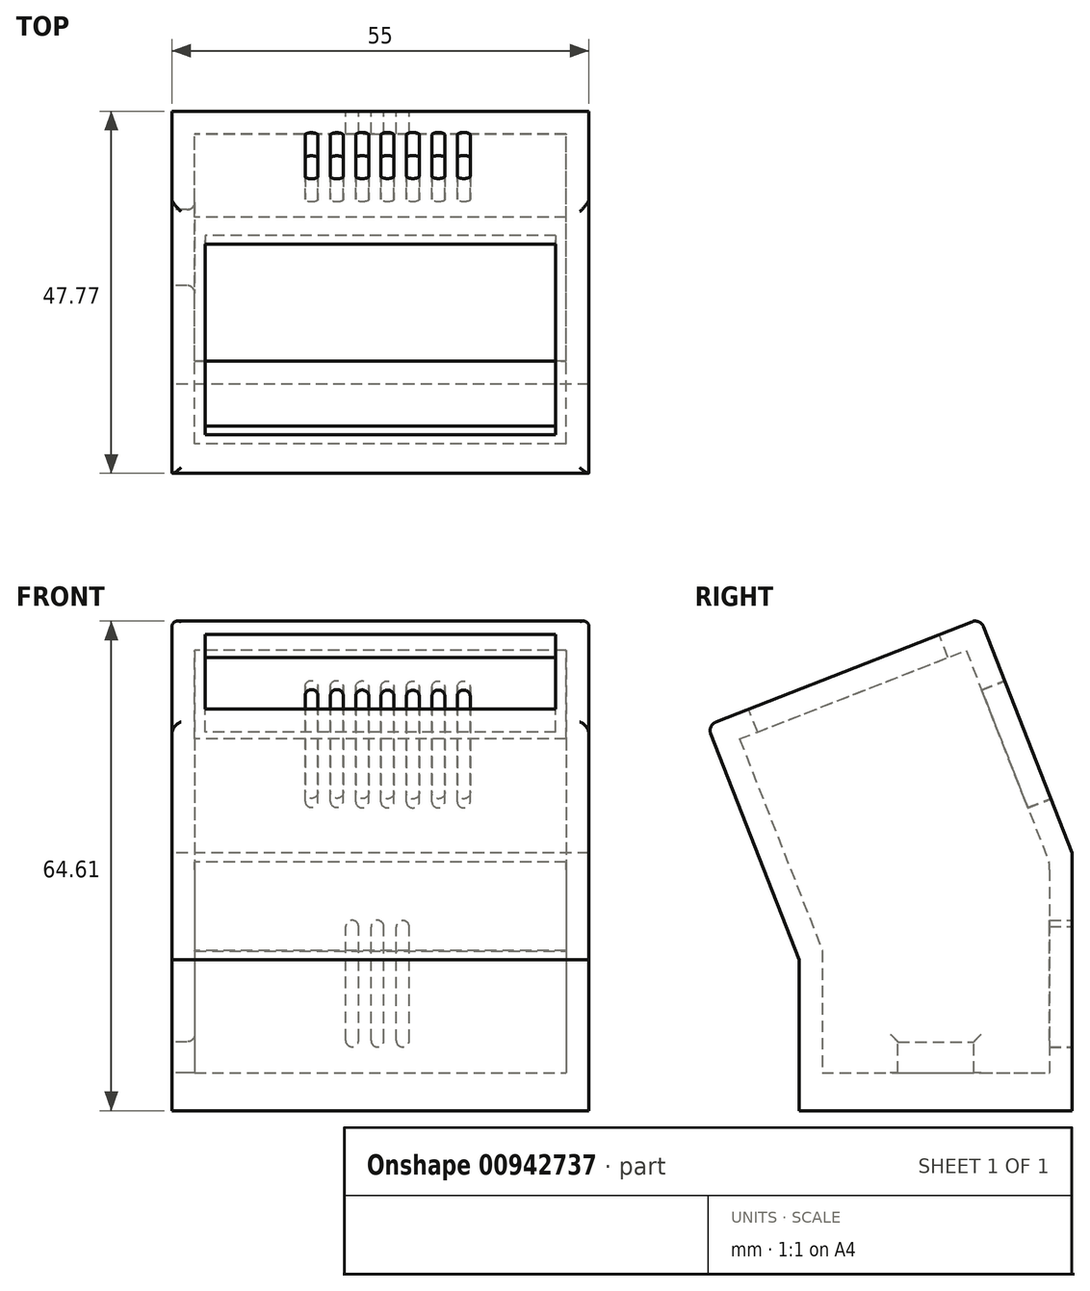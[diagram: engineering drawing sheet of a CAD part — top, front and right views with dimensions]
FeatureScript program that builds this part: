
annotation { "Feature Type Name" : "Feature", "Feature Type Description" : "" }
export const myFeature = defineFeature(function(context is Context, id is Id, definition is map)
    precondition{}
    {
        {
            var Q0;
            Q0=qCreatedBy(makeId("Top.planeOp"),FACE);
            var sketch = newSketch(context, id + "F0", { "sketchPlane" : qUnion([Q0])});
            skLineSegment(sketch, "E0.bottom", {"start": v(27.5, -18) * mm, "end": v(-27.5, -18) * mm});
            skLineSegment(sketch, "E0.top", {"start": v(27.5, 18) * mm, "end": v(-27.5, 18) * mm});
            skLineSegment(sketch, "E0.left", {"start": v(27.5, -18) * mm, "end": v(27.5, 18) * mm});
            skLineSegment(sketch, "E0.right", {"start": v(-27.5, -18) * mm, "end": v(-27.5, 18) * mm});
            skLineSegment(sketch, "E1.bottom", {"start": v(24.5, 15) * mm, "end": v(-24.5, 15) * mm});
            skLineSegment(sketch, "E1.top", {"start": v(24.5, -15) * mm, "end": v(-24.5, -15) * mm});
            skLineSegment(sketch, "E1.left", {"start": v(24.5, 15) * mm, "end": v(24.5, -15) * mm});
            skLineSegment(sketch, "E1.right", {"start": v(-24.5, 15) * mm, "end": v(-24.5, -15) * mm});
            skPoint(sketch, "E1.middle", {"position": v(0, 0) * mm});
            skSolve(sketch);
        }
        {
            var Q0;
            Q0 = qSketchRegion(id + "F0", true);
            extrude(context, id + "F1", {"entities" : qUnion([Q0]), "depth" : 34 * mm, "offsetDistance" : 25 * mm});
        }
        {
            var Q0;
            Q0=makeQuery(id+"F1.opExtrude","CAP_EDGE",EDGE,{"disambiguationData":[OSD([sQuery(id+"F0.wireOp",EDGE,"E0.bottom")])],"isStart":false});
            chamfer(context, id + "F2", {"entities" : qUnion([Q0]), "chamferType" : ChamferType.TWO_OFFSETS, "width1" : 14.1 * mm, "oppositeDirection" : false, "width2" : 36 * mm, "tangentPropagation" : true});
        }
        {
            var Q0;
            Q0=makeQuery(id+"F2.opChamfer","BLEND_FACE",FACE,{"disambiguationData":[OSD([sQuery(id+"F0.wireOp",EDGE,"E0.bottom")])]});
            var sketch = newSketch(context, id + "F3", { "sketchPlane" : qUnion([Q0])});
            skLineSegment(sketch, "E2.bottom", {"start": v(-27.5, 29.16) * mm, "end": v(27.5, 29.16) * mm});
            skLineSegment(sketch, "E2.top", {"start": v(-27.5, -9.5) * mm, "end": v(27.5, -9.5) * mm});
            skLineSegment(sketch, "E2.left", {"start": v(-27.5, 29.16) * mm, "end": v(-27.5, -9.5) * mm});
            skLineSegment(sketch, "E2.right", {"start": v(27.5, 29.16) * mm, "end": v(27.5, -9.5) * mm});
            skLineSegment(sketch, "E3.bottom", {"start": v(24.5, -6.22) * mm, "end": v(-24.5, -6.22) * mm});
            skLineSegment(sketch, "E3.top", {"start": v(24.5, 25.88) * mm, "end": v(-24.5, 25.88) * mm});
            skLineSegment(sketch, "E3.left", {"start": v(24.5, -6.22) * mm, "end": v(24.5, 25.88) * mm});
            skLineSegment(sketch, "E3.right", {"start": v(-24.5, -6.22) * mm, "end": v(-24.5, 25.88) * mm});
            skPoint(sketch, "E3.middle", {"position": v(0, 9.83) * mm});
            skPoint(sketch, "E3.middle.positionSnap0", {"position": v(-27.5, 9.83) * mm});
            skPoint(sketch, "E3.middle.positionSnap1", {"position": v(0, 29.16) * mm});
            skPoint(sketch, "E3.centerSnap0", {"position": v(-27.5, 9.83) * mm});
            skPoint(sketch, "E3.centerSnap1", {"position": v(0, 29.16) * mm});
            skSolve(sketch);
        }
        {
            var Q0;
            Q0 = qSketchRegion(id + "F3", true);
            extrude(context, id + "F4", {"entities" : qUnion([Q0]), "operationType" : NewBodyOperationType.ADD, "depth" : 30 * mm, "offsetDistance" : 25 * mm});
        }
        {
            var Q0;
            Q0=makeQuery(id+"F1.opExtrude","CAP_FACE",FACE,{"disambiguationData":[OSD([sQuery(id+"F0.wireOp",EDGE,"E0.bottom"),sQuery(id+"F0.wireOp",EDGE,"E0.top"),sQuery(id+"F0.wireOp",EDGE,"E0.left"),sQuery(id+"F0.wireOp",EDGE,"E0.right")])],"isStart":true});
            var sketch = newSketch(context, id + "F5", { "sketchPlane" : qUnion([Q0])});
            skLineSegment(sketch, "E4.bottom", {"start": v(24.5, -15) * mm, "end": v(-24.5, -15) * mm});
            skLineSegment(sketch, "E4.top", {"start": v(24.5, 15) * mm, "end": v(-24.5, 15) * mm});
            skLineSegment(sketch, "E4.left", {"start": v(24.5, -15) * mm, "end": v(24.5, 15) * mm});
            skLineSegment(sketch, "E4.right", {"start": v(-24.5, -15) * mm, "end": v(-24.5, 15) * mm});
            skPoint(sketch, "E4.middle", {"position": v(0, 0) * mm});
            skSolve(sketch);
        }
        {
            var Q0;
            {var subQ10=sQuery(id+"F5.wireOp",EDGE,"E4.bottom");Q0=makeQuery(id+"F5.imprint","IMPRINT",FACE,{"disambiguationData":[TD([[makeQuery(id+"F5.imprint","IMPRINT",EDGE,{"derivedFrom":subQ10}),1.0]])]});}
            var Q1;
            Q1 = qSketchRegion(id + "F5", true);
            extrude(context, id + "F6", {"entities" : qUnion([Q0, Q1]), "operationType" : NewBodyOperationType.ADD, "oppositeDirection" : true, "depth" : 5 * mm, "offsetDistance" : 25 * mm});
        }
        {
            var Q0;
            Q0=makeQuery(id+"F4.boolean.opBoolean","MERGE",FACE,{"derivedFrom":[makeQuery(id+"F1.opExtrude","SWEPT_FACE",FACE,{"disambiguationData":[OSD([sQuery(id+"F0.wireOp",EDGE,"E0.right")])]}),makeQuery(id+"F4.opExtrude","SWEPT_FACE",FACE,{"disambiguationData":[OSD([sQuery(id+"F3.wireOp",EDGE,"E2.left")])]})]});
            var sketch = newSketch(context, id + "F7", { "sketchPlane" : qUnion([Q0])});
            skLineSegment(sketch, "E5.bottom", {"start": v(5, 5) * mm, "end": v(-5, 5) * mm});
            skLineSegment(sketch, "E5.top", {"start": v(5, 9.08) * mm, "end": v(-5, 9.08) * mm});
            skLineSegment(sketch, "E5.left", {"start": v(5, 5) * mm, "end": v(5, 9.08) * mm});
            skLineSegment(sketch, "E5.right", {"start": v(-5, 5) * mm, "end": v(-5, 9.08) * mm});
            skPoint(sketch, "E5.middle", {"position": v(0, 7.04) * mm});
            skSolve(sketch);
        }
        {
            var Q0;
            Q0 = qSketchRegion(id + "F7", true);
            extrude(context, id + "F8", {"entities" : qUnion([Q0]), "operationType" : NewBodyOperationType.REMOVE, "oppositeDirection" : true, "depth" : 17.9 * mm, "offsetDistance" : 25 * mm});
        }
        {
            var Q0;
            Q0=makeQuery(id+"F8.boolean.opBoolean","INTERSECT",EDGE,{"derivedFrom":[makeQuery(id+"F4.boolean.opBoolean","MERGE",FACE,{"derivedFrom":[makeQuery(id+"F1.opExtrude","SWEPT_FACE",FACE,{"disambiguationData":[OSD([sQuery(id+"F0.wireOp",EDGE,"E1.right")])]}),makeQuery(id+"F4.opExtrude","SWEPT_FACE",FACE,{"disambiguationData":[OSD([sQuery(id+"F3.wireOp",EDGE,"E3.right")])]})]}),makeQuery(id+"F8.opExtrude","SWEPT_FACE",FACE,{"disambiguationData":[OSD([sQuery(id+"F7.wireOp",EDGE,"E5.right")])]})]});
            var Q1;
            Q1=makeQuery(id+"F8.boolean.opBoolean","INTERSECT",EDGE,{"derivedFrom":[makeQuery(id+"F4.boolean.opBoolean","MERGE",FACE,{"derivedFrom":[makeQuery(id+"F1.opExtrude","SWEPT_FACE",FACE,{"disambiguationData":[OSD([sQuery(id+"F0.wireOp",EDGE,"E1.right")])]}),makeQuery(id+"F4.opExtrude","SWEPT_FACE",FACE,{"disambiguationData":[OSD([sQuery(id+"F3.wireOp",EDGE,"E3.right")])]})]}),makeQuery(id+"F8.opExtrude","SWEPT_FACE",FACE,{"disambiguationData":[OSD([sQuery(id+"F7.wireOp",EDGE,"E5.left")])]})]});
            var Q2;
            Q2=makeQuery(id+"F8.boolean.opBoolean","INTERSECT",EDGE,{"derivedFrom":[makeQuery(id+"F4.boolean.opBoolean","MERGE",FACE,{"derivedFrom":[makeQuery(id+"F1.opExtrude","SWEPT_FACE",FACE,{"disambiguationData":[OSD([sQuery(id+"F0.wireOp",EDGE,"E1.right")])]}),makeQuery(id+"F4.opExtrude","SWEPT_FACE",FACE,{"disambiguationData":[OSD([sQuery(id+"F3.wireOp",EDGE,"E3.right")])]})]}),makeQuery(id+"F8.opExtrude","SWEPT_FACE",FACE,{"disambiguationData":[OSD([sQuery(id+"F7.wireOp",EDGE,"E5.top")])]})]});
            var Q3;
            Q3=makeQuery(id+"F8.boolean.opBoolean","COPY",EDGE,{"derivedFrom":makeQuery(id+"F8.opExtrude","CAP_EDGE",EDGE,{"disambiguationData":[OSD([sQuery(id+"F7.wireOp",EDGE,"E5.right")])],"isStart":true})});
            var Q4;
            Q4=makeQuery(id+"F8.boolean.opBoolean","COPY",EDGE,{"derivedFrom":makeQuery(id+"F8.opExtrude","CAP_EDGE",EDGE,{"disambiguationData":[OSD([sQuery(id+"F7.wireOp",EDGE,"E5.top")])],"isStart":true})});
            var Q5;
            Q5=makeQuery(id+"F8.boolean.opBoolean","COPY",EDGE,{"derivedFrom":makeQuery(id+"F8.opExtrude","CAP_EDGE",EDGE,{"disambiguationData":[OSD([sQuery(id+"F7.wireOp",EDGE,"E5.left")])],"isStart":true})});
            var Q6;
            Q6=makeQuery(id+"F8.boolean.opBoolean","COPY",EDGE,{"derivedFrom":makeQuery(id+"F8.opExtrude","CAP_EDGE",EDGE,{"disambiguationData":[OSD([sQuery(id+"F7.wireOp",EDGE,"E5.bottom")])],"isStart":true})});
            fillet(context, id + "F9", {"entities" : qUnion([Q0, Q1, Q2, Q3, Q4, Q5, Q6]), "radius" : 1 * mm, "tangentPropagation" : true, "allowEdgeOverflow" : false});
        }
        {
            var Q0;
            Q0=makeQuery(id+"F4.opExtrude","CAP_FACE",FACE,{"disambiguationData":[OSD([sQuery(id+"F3.wireOp",EDGE,"E2.bottom"),sQuery(id+"F3.wireOp",EDGE,"E2.top"),sQuery(id+"F3.wireOp",EDGE,"E2.left"),sQuery(id+"F3.wireOp",EDGE,"E2.right"),sQuery(id+"F3.wireOp",EDGE,"E3.bottom"),sQuery(id+"F3.wireOp",EDGE,"E3.top"),sQuery(id+"F3.wireOp",EDGE,"E3.left"),sQuery(id+"F3.wireOp",EDGE,"E3.right")])],"isStart":false});
            var sketch = newSketch(context, id + "F10", { "sketchPlane" : qUnion([Q0])});
            skLineSegment(sketch, "E6.bottom", {"start": v(-27.5, 29.16) * mm, "end": v(27.5, 29.16) * mm});
            skLineSegment(sketch, "E6.top", {"start": v(-27.5, -9.5) * mm, "end": v(27.5, -9.5) * mm});
            skLineSegment(sketch, "E6.left", {"start": v(-27.5, 29.16) * mm, "end": v(-27.5, -9.5) * mm});
            skLineSegment(sketch, "E6.right", {"start": v(27.5, 29.16) * mm, "end": v(27.5, -9.5) * mm});
            skSolve(sketch);
        }
        {
            var Q0;
            Q0 = qSketchRegion(id + "F10", true);
            extrude(context, id + "F11", {"entities" : qUnion([Q0]), "operationType" : NewBodyOperationType.ADD, "depth" : 3.25 * mm, "offsetDistance" : 25 * mm});
        }
        {
            var Q0;
            Q0=makeQuery(id+"F11.opExtrude","CAP_FACE",FACE,{"disambiguationData":[OSD([sQuery(id+"F10.wireOp",EDGE,"E6.bottom"),sQuery(id+"F10.wireOp",EDGE,"E6.top"),sQuery(id+"F10.wireOp",EDGE,"E6.left"),sQuery(id+"F10.wireOp",EDGE,"E6.right")])],"isStart":false});
            var sketch = newSketch(context, id + "F12", { "sketchPlane" : qUnion([Q0])});
            skLineSegment(sketch, "E7.bottom", {"start": v(23.12, -3.69) * mm, "end": v(-23.13, -3.69) * mm});
            skLineSegment(sketch, "E7.top", {"start": v(23.12, 23.31) * mm, "end": v(-23.13, 23.31) * mm});
            skLineSegment(sketch, "E7.left", {"start": v(23.12, -3.69) * mm, "end": v(23.12, 23.31) * mm});
            skLineSegment(sketch, "E7.right", {"start": v(-23.13, -3.69) * mm, "end": v(-23.13, 23.31) * mm});
            skPoint(sketch, "E7.middle", {"position": v(0, 9.81) * mm});
            skSolve(sketch);
        }
        {
            var Q0;
            Q0 = qSketchRegion(id + "F12", true);
            extrude(context, id + "F13", {"entities" : qUnion([Q0]), "operationType" : NewBodyOperationType.REMOVE, "oppositeDirection" : true, "depth" : 6.9 * mm, "offsetDistance" : 25 * mm});
        }
        {
            var Q0;
            Q0=makeQuery(id+"F11.opExtrude","CAP_EDGE",EDGE,{"disambiguationData":[OSD([sQuery(id+"F10.wireOp",EDGE,"E6.left")])],"isStart":false});
            var Q1;
            Q1=makeQuery(id+"F11.opExtrude","CAP_EDGE",EDGE,{"disambiguationData":[OSD([sQuery(id+"F10.wireOp",EDGE,"E6.bottom")])],"isStart":false});
            var Q2;
            Q2=makeQuery(id+"F11.opExtrude","CAP_EDGE",EDGE,{"disambiguationData":[OSD([sQuery(id+"F10.wireOp",EDGE,"E6.right")])],"isStart":false});
            var Q3;
            Q3=makeQuery(id+"F11.opExtrude","CAP_EDGE",EDGE,{"disambiguationData":[OSD([sQuery(id+"F10.wireOp",EDGE,"E6.top")])],"isStart":false});
            fillet(context, id + "F14", {"entities" : qUnion([Q0, Q1, Q2, Q3]), "radius" : 1.2 * mm, "tangentPropagation" : true, "allowEdgeOverflow" : false});
        }
        {
            var Q0;
            Q0=makeQuery(id+"F2.opChamfer","BLEND_EDGE",EDGE,{"blendedFrom":[makeQuery(id+"F1.opExtrude","CAP_EDGE",EDGE,{"disambiguationData":[OSD([sQuery(id+"F0.wireOp",EDGE,"E0.bottom")])],"isStart":false}),makeQuery(id+"F1.opExtrude","SWEPT_FACE",FACE,{"disambiguationData":[OSD([sQuery(id+"F0.wireOp",EDGE,"E1.bottom")])]})],"blendedInto":[makeQuery(id+"F1.opExtrude","SWEPT_FACE",FACE,{"disambiguationData":[OSD([sQuery(id+"F0.wireOp",EDGE,"E1.bottom")])]})]});
            fillet(context, id + "F15", {"entities" : qUnion([Q0]), "radius" : 9.17 * mm, "tangentPropagation" : true, "allowEdgeOverflow" : false});
        }
        {
            var Q0;
            Q0=makeQuery(id+"F11.boolean.opBoolean","MERGE",FACE,{"derivedFrom":[makeQuery(id+"F4.opExtrude","SWEPT_FACE",FACE,{"disambiguationData":[OSD([sQuery(id+"F3.wireOp",EDGE,"E2.bottom")])]}),makeQuery(id+"F11.opExtrude","SWEPT_FACE",FACE,{"disambiguationData":[OSD([sQuery(id+"F10.wireOp",EDGE,"E6.bottom")])]})]});
            var sketch = newSketch(context, id + "F16", { "sketchPlane" : qUnion([Q0])});
            skLineSegment(sketch, "E8.bottom", {"start": v(-0.08, 48.62) * mm, "end": v(-1.78, 48.62) * mm});
            skLineSegment(sketch, "E8.top", {"start": v(-0.08, 33.62) * mm, "end": v(-1.78, 33.62) * mm});
            skLineSegment(sketch, "E8.left", {"start": v(-0.08, 48.62) * mm, "end": v(-0.08, 33.62) * mm});
            skLineSegment(sketch, "E8.right", {"start": v(-1.78, 48.62) * mm, "end": v(-1.78, 33.62) * mm});
            skPoint(sketch, "E8.middle", {"position": v(6.02, 41.12) * mm});
            skLineSegment(sketch, "E9.bottom", {"start": v(3.26, 48.64) * mm, "end": v(1.55, 48.64) * mm});
            skLineSegment(sketch, "E9.top", {"start": v(3.26, 33.64) * mm, "end": v(1.55, 33.64) * mm});
            skLineSegment(sketch, "E9.left", {"start": v(3.26, 48.64) * mm, "end": v(3.26, 33.64) * mm});
            skLineSegment(sketch, "E9.right", {"start": v(1.55, 48.64) * mm, "end": v(1.55, 33.64) * mm});
            skPoint(sketch, "E9.middle", {"position": v(2.4, 41.14) * mm});
            skLineSegment(sketch, "E10.bottom", {"start": v(6.6, 48.7) * mm, "end": v(4.9, 48.7) * mm});
            skLineSegment(sketch, "E10.top", {"start": v(6.6, 33.7) * mm, "end": v(4.9, 33.7) * mm});
            skLineSegment(sketch, "E10.left", {"start": v(6.6, 48.7) * mm, "end": v(6.6, 33.7) * mm});
            skLineSegment(sketch, "E10.right", {"start": v(4.9, 48.7) * mm, "end": v(4.9, 33.7) * mm});
            skLineSegment(sketch, "E11.bottom", {"start": v(9.94, 48.7) * mm, "end": v(8.24, 48.7) * mm});
            skLineSegment(sketch, "E11.top", {"start": v(9.94, 33.7) * mm, "end": v(8.24, 33.7) * mm});
            skLineSegment(sketch, "E11.left", {"start": v(9.94, 48.7) * mm, "end": v(9.94, 33.7) * mm});
            skLineSegment(sketch, "E11.right", {"start": v(8.24, 48.7) * mm, "end": v(8.24, 33.7) * mm});
            skLineSegment(sketch, "E12.bottom", {"start": v(-3.42, 48.6) * mm, "end": v(-5.13, 48.6) * mm});
            skLineSegment(sketch, "E12.top", {"start": v(-3.42, 33.6) * mm, "end": v(-5.13, 33.6) * mm});
            skLineSegment(sketch, "E12.left", {"start": v(-3.42, 48.6) * mm, "end": v(-3.42, 33.6) * mm});
            skLineSegment(sketch, "E12.right", {"start": v(-5.13, 48.6) * mm, "end": v(-5.13, 33.6) * mm});
            skPoint(sketch, "E12.middle", {"position": v(2.4, 41.1) * mm});
            skLineSegment(sketch, "E13.bottom", {"start": v(-6.8, 48.62) * mm, "end": v(-8.5, 48.62) * mm});
            skLineSegment(sketch, "E13.top", {"start": v(-6.8, 33.62) * mm, "end": v(-8.5, 33.62) * mm});
            skLineSegment(sketch, "E13.left", {"start": v(-6.8, 48.62) * mm, "end": v(-6.8, 33.62) * mm});
            skLineSegment(sketch, "E13.right", {"start": v(-8.5, 48.62) * mm, "end": v(-8.5, 33.62) * mm});
            skPoint(sketch, "E13.middle", {"position": v(2.4, 41.12) * mm});
            skLineSegment(sketch, "E14.bottom", {"start": v(-10.14, 48.62) * mm, "end": v(-11.84, 48.62) * mm});
            skLineSegment(sketch, "E14.top", {"start": v(-10.14, 33.62) * mm, "end": v(-11.84, 33.62) * mm});
            skLineSegment(sketch, "E14.left", {"start": v(-10.14, 48.62) * mm, "end": v(-10.14, 33.62) * mm});
            skLineSegment(sketch, "E14.right", {"start": v(-11.84, 48.62) * mm, "end": v(-11.84, 33.62) * mm});
            skArc(sketch, "E15", {"start": v(-10.14, 48.62) * mm, "mid": v(-10.99, 49.47) * mm, "end": v(-11.84, 48.62) * mm});
            skArc(sketch, "E16", {"start": v(-11.84, 33.62) * mm, "mid": v(-10.99, 32.77) * mm, "end": v(-10.14, 33.62) * mm});
            skArc(sketch, "E17", {"start": v(-6.8, 48.62) * mm, "mid": v(-7.65, 49.47) * mm, "end": v(-8.5, 48.62) * mm});
            skPoint(sketch, "E17.midSnap0", {"position": v(-7.65, 48.62) * mm});
            skPoint(sketch, "E17.midSnap1", {"position": v(-10.99, 49.47) * mm});
            skArc(sketch, "E18", {"start": v(-8.5, 33.62) * mm, "mid": v(-7.65, 32.77) * mm, "end": v(-6.8, 33.62) * mm});
            skArc(sketch, "E19", {"start": v(-3.42, 48.6) * mm, "mid": v(-4.28, 49.46) * mm, "end": v(-5.13, 48.6) * mm});
            skArc(sketch, "E20", {"start": v(-5.13, 33.6) * mm, "mid": v(-4.28, 32.75) * mm, "end": v(-3.42, 33.6) * mm});
            skArc(sketch, "E21", {"start": v(-0.08, 48.62) * mm, "mid": v(-0.93, 49.47) * mm, "end": v(-1.78, 48.62) * mm});
            skArc(sketch, "E22", {"start": v(-1.78, 33.62) * mm, "mid": v(-0.93, 32.77) * mm, "end": v(-0.08, 33.62) * mm});
            skArc(sketch, "E23", {"start": v(3.26, 48.64) * mm, "mid": v(2.4, 49.5) * mm, "end": v(1.55, 48.64) * mm});
            skArc(sketch, "E24", {"start": v(1.55, 33.64) * mm, "mid": v(2.4, 32.79) * mm, "end": v(3.26, 33.64) * mm});
            skArc(sketch, "E25", {"start": v(4.9, 33.7) * mm, "mid": v(5.75, 32.84) * mm, "end": v(6.6, 33.7) * mm});
            skArc(sketch, "E26", {"start": v(6.6, 48.7) * mm, "mid": v(5.75, 49.54) * mm, "end": v(4.9, 48.7) * mm});
            skArc(sketch, "E27", {"start": v(9.94, 48.7) * mm, "mid": v(9.1, 49.54) * mm, "end": v(8.24, 48.7) * mm});
            skPoint(sketch, "E27.midSnap0", {"position": v(9.1, 48.7) * mm});
            skPoint(sketch, "E27.midSnap1", {"position": v(5.63, 49.54) * mm});
            skArc(sketch, "E28", {"start": v(8.24, 33.7) * mm, "mid": v(9.1, 32.84) * mm, "end": v(9.94, 33.7) * mm});
            skSolve(sketch);
        }
        {
            var Q0;
            Q0 = qSketchRegion(id + "F16", true);
            extrude(context, id + "F17", {"entities" : qUnion([Q0]), "operationType" : NewBodyOperationType.REMOVE, "oppositeDirection" : true, "depth" : 5.9 * mm, "offsetDistance" : 25 * mm});
        }
        {
            var Q0;
            Q0=makeQuery(id+"F1.opExtrude","SWEPT_FACE",FACE,{"disambiguationData":[OSD([sQuery(id+"F0.wireOp",EDGE,"E0.top")])]});
            var sketch = newSketch(context, id + "F18", { "sketchPlane" : qUnion([Q0])});
            skLineSegment(sketch, "E29.bottom", {"start": v(1.24, 24.25) * mm, "end": v(-0.46, 24.25) * mm});
            skLineSegment(sketch, "E29.top", {"start": v(1.24, 9.25) * mm, "end": v(-0.46, 9.25) * mm});
            skLineSegment(sketch, "E29.left", {"start": v(1.24, 24.25) * mm, "end": v(1.24, 9.25) * mm});
            skLineSegment(sketch, "E29.right", {"start": v(-0.46, 24.25) * mm, "end": v(-0.46, 9.25) * mm});
            skPoint(sketch, "E29.middle", {"position": v(0.39, 16.75) * mm});
            skLineSegment(sketch, "E30.bottom", {"start": v(4.59, 24.27) * mm, "end": v(2.88, 24.27) * mm});
            skLineSegment(sketch, "E30.top", {"start": v(4.59, 9.27) * mm, "end": v(2.88, 9.27) * mm});
            skLineSegment(sketch, "E30.left", {"start": v(4.59, 24.27) * mm, "end": v(4.59, 9.27) * mm});
            skLineSegment(sketch, "E30.right", {"start": v(2.88, 24.27) * mm, "end": v(2.88, 9.27) * mm});
            skPoint(sketch, "E30.middle", {"position": v(3.73, 16.77) * mm});
            skLineSegment(sketch, "E31.bottom", {"start": v(-2.1, 24.24) * mm, "end": v(-3.8, 24.24) * mm});
            skLineSegment(sketch, "E31.top", {"start": v(-2.1, 9.24) * mm, "end": v(-3.8, 9.24) * mm});
            skLineSegment(sketch, "E31.left", {"start": v(-2.1, 24.24) * mm, "end": v(-2.1, 9.24) * mm});
            skLineSegment(sketch, "E31.right", {"start": v(-3.8, 24.24) * mm, "end": v(-3.8, 9.24) * mm});
            skArc(sketch, "E32", {"start": v(-2.1, 24.24) * mm, "mid": v(-2.95, 25.1) * mm, "end": v(-3.8, 24.24) * mm});
            skArc(sketch, "E33", {"start": v(1.24, 24.25) * mm, "mid": v(0.39, 25.1) * mm, "end": v(-0.46, 24.25) * mm});
            skArc(sketch, "E34", {"start": v(4.59, 24.27) * mm, "mid": v(3.73, 25.1) * mm, "end": v(2.88, 24.27) * mm});
            skPoint(sketch, "E34.midSnap0", {"position": v(3.73, 24.27) * mm});
            skPoint(sketch, "E34.midSnap1", {"position": v(0.39, 25.1) * mm});
            skArc(sketch, "E35", {"start": v(-3.8, 9.24) * mm, "mid": v(-2.95, 8.39) * mm, "end": v(-2.1, 9.24) * mm});
            skArc(sketch, "E36", {"start": v(-0.46, 9.25) * mm, "mid": v(0.39, 8.4) * mm, "end": v(1.24, 9.25) * mm});
            skArc(sketch, "E37", {"start": v(2.88, 9.27) * mm, "mid": v(3.73, 8.42) * mm, "end": v(4.59, 9.27) * mm});
            skSolve(sketch);
        }
        {
            var Q0;
            Q0 = qSketchRegion(id + "F18", true);
            extrude(context, id + "F19", {"entities" : qUnion([Q0]), "operationType" : NewBodyOperationType.REMOVE, "oppositeDirection" : true, "depth" : 3.7 * mm, "offsetDistance" : 25 * mm});
        }
    });
